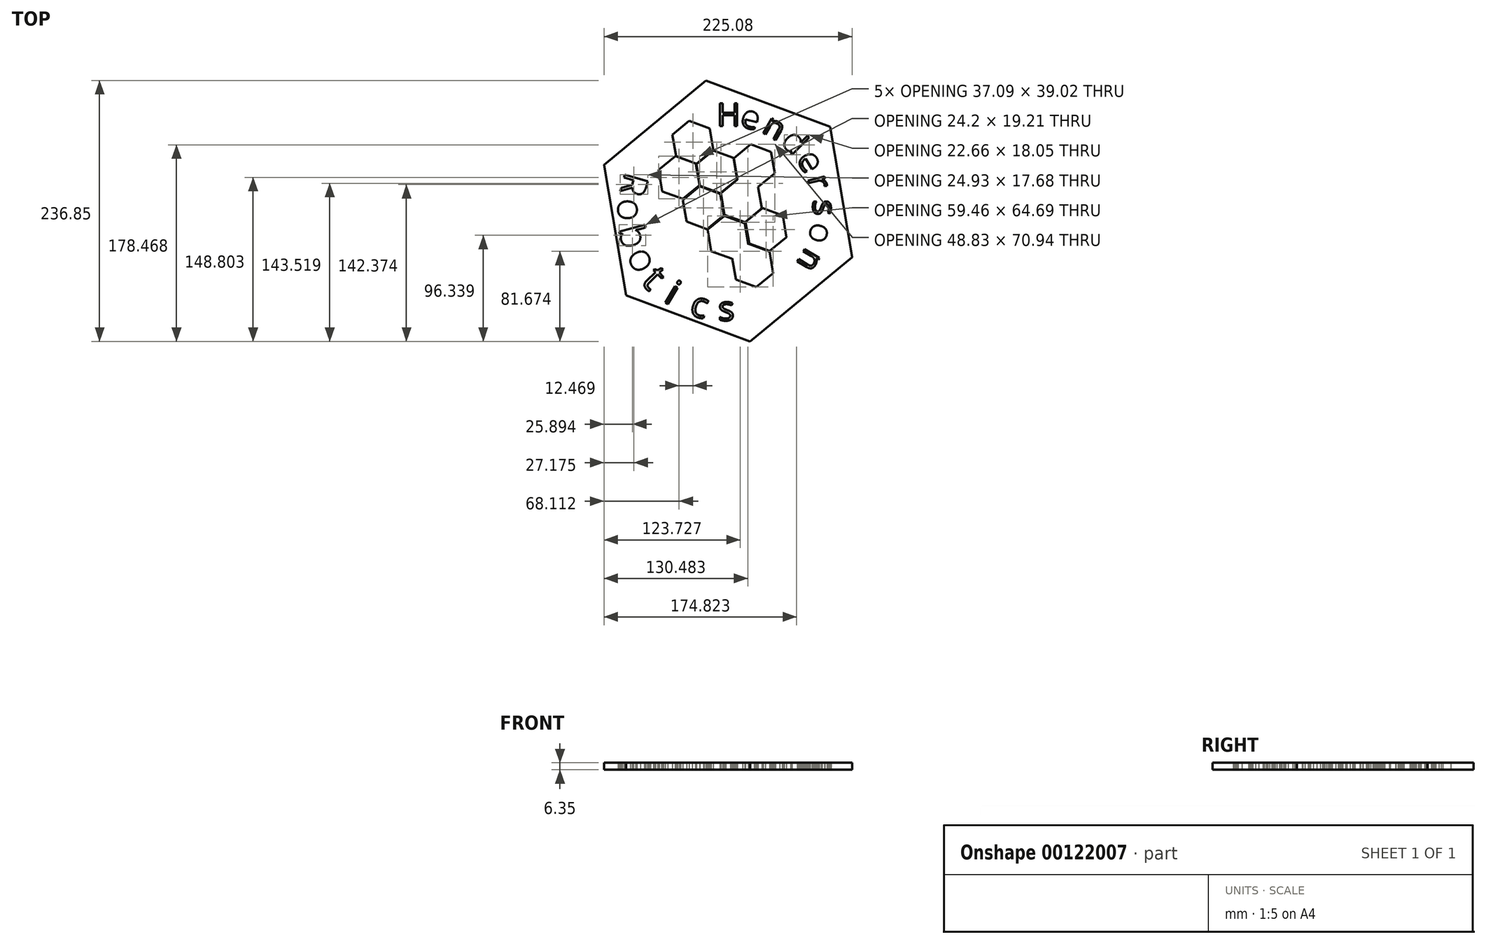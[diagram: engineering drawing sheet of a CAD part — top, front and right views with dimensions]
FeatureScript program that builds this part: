
annotation { "Feature Type Name" : "Feature", "Feature Type Description" : "" }
export const myFeature = defineFeature(function(context is Context, id is Id, definition is map)
    precondition{}
    {
        {
            var Q0;
            Q0=qCreatedBy(makeId("Top.planeOp"),FACE);
            var sketch = newSketch(context, id + "F0", { "sketchPlane" : qUnion([Q0])});
            skLineSegment(sketch, "E0.5.0", {"start": v(-77.17, 34.08) * mm, "end": v(-71.91, 53.7) * mm});
            skLineSegment(sketch, "E0.7.0", {"start": v(-71.91, -5.87) * mm, "end": v(-77.17, 13.76) * mm});
            skPoint(sketch, "E0.center", {"position": v(0, 23.92) * mm});
            skText(sketch, "E1", { "text": "H", "fontName": "OpenSans-Regular.ttf"});
            skText(sketch, "E2", { "text": "e", "fontName": "OpenSans-Regular.ttf"});
            skText(sketch, "E3", { "text": "n", "fontName": "OpenSans-Regular.ttf"});
            skText(sketch, "E4", { "text": "d", "fontName": "OpenSans-Regular.ttf"});
            skText(sketch, "E5", { "text": "e", "fontName": "OpenSans-Regular.ttf"});
            skText(sketch, "E6", { "text": "r", "fontName": "OpenSans-Regular.ttf"});
            skText(sketch, "E7", { "text": "s", "fontName": "OpenSans-Regular.ttf"});
            skText(sketch, "E8", { "text": "o", "fontName": "OpenSans-Regular.ttf"});
            skText(sketch, "E9", { "text": "s", "fontName": "OpenSans-Regular.ttf"});
            skText(sketch, "E10", { "text": "c", "fontName": "OpenSans-Regular.ttf"});
            skText(sketch, "E11", { "text": "i", "fontName": "OpenSans-Regular.ttf"});
            skText(sketch, "E12", { "text": "t", "fontName": "OpenSans-Regular.ttf"});
            skText(sketch, "E13", { "text": "o", "fontName": "OpenSans-Regular.ttf"});
            skText(sketch, "E14", { "text": "b", "fontName": "OpenSans-Regular.ttf"});
            skText(sketch, "E15", { "text": "o", "fontName": "OpenSans-Regular.ttf"});
            skText(sketch, "E16", { "text": "R", "fontName": "OpenSans-Regular.ttf"});
            skText(sketch, "E17", { "text": "n", "fontName": "OpenSans-Regular.ttf"});
            skCircle(sketch, "E18.cCircle", {"center": v(0, 23.92) * mm, "radius": 104 * mm, "construction": true});
            skLineSegment(sketch, "E18.0", {"start": v(92.58, 100.41) * mm, "end": v(112.54, -18.01) * mm});
            skLineSegment(sketch, "E18.1", {"start": v(112.54, -18.01) * mm, "end": v(19.96, -94.5) * mm});
            skLineSegment(sketch, "E18.2", {"start": v(19.96, -94.5) * mm, "end": v(-92.58, -52.58) * mm});
            skLineSegment(sketch, "E18.3", {"start": v(-92.58, -52.58) * mm, "end": v(-112.54, 65.85) * mm});
            skLineSegment(sketch, "E18.4", {"start": v(-112.54, 65.85) * mm, "end": v(-19.96, 142.34) * mm});
            skLineSegment(sketch, "E18.5", {"start": v(-19.96, 142.34) * mm, "end": v(92.58, 100.41) * mm});
            skPoint(sketch, "E18.0.midPoint", {"position": v(102.56, 41.2) * mm});
            skCircle(sketch, "E19.cCircle", {"center": v(-10.25, 59.37) * mm, "radius": 17.14 * mm, "construction": true});
            skLineSegment(sketch, "E19.0", {"start": v(8.29, 52.47) * mm, "end": v(-6.96, 39.86) * mm});
            skLineSegment(sketch, "E19.1", {"start": v(-6.96, 39.86) * mm, "end": v(-25.5, 46.77) * mm});
            skLineSegment(sketch, "E19.2", {"start": v(-25.5, 46.77) * mm, "end": v(-28.8, 66.28) * mm});
            skLineSegment(sketch, "E19.3", {"start": v(-28.8, 66.28) * mm, "end": v(-13.54, 78.89) * mm});
            skLineSegment(sketch, "E19.4", {"start": v(-13.54, 78.89) * mm, "end": v(5, 71.98) * mm});
            skLineSegment(sketch, "E19.5", {"start": v(5, 71.98) * mm, "end": v(8.29, 52.47) * mm});
            skCircle(sketch, "E20.cCircle", {"center": v(12.07, 33.05) * mm, "radius": 17.14 * mm, "construction": true});
            skLineSegment(sketch, "E20.0", {"start": v(30.61, 26.14) * mm, "end": v(15.36, 13.54) * mm});
            skLineSegment(sketch, "E20.1", {"start": v(15.36, 13.54) * mm, "end": v(-3.18, 20.44) * mm});
            skLineSegment(sketch, "E20.2", {"start": v(-3.18, 20.44) * mm, "end": v(-6.47, 39.96) * mm});
            skLineSegment(sketch, "E20.3", {"start": v(-6.47, 39.96) * mm, "end": v(8.78, 52.56) * mm});
            skLineSegment(sketch, "E20.4", {"start": v(8.78, 52.56) * mm, "end": v(27.32, 45.65) * mm});
            skLineSegment(sketch, "E20.5", {"start": v(27.32, 45.65) * mm, "end": v(30.61, 26.14) * mm});
            skCircle(sketch, "E21.cCircle", {"center": v(0, 0) * mm, "radius": 17.14 * mm, "construction": true});
            skLineSegment(sketch, "E21.0", {"start": v(15.25, 12.6) * mm, "end": v(18.54, -6.9) * mm});
            skLineSegment(sketch, "E21.1", {"start": v(18.54, -6.9) * mm, "end": v(3.3, -19.51) * mm});
            skLineSegment(sketch, "E21.2", {"start": v(3.3, -19.51) * mm, "end": v(-15.25, -12.6) * mm});
            skLineSegment(sketch, "E21.3", {"start": v(-15.25, -12.6) * mm, "end": v(-18.54, 6.9) * mm});
            skLineSegment(sketch, "E21.4", {"start": v(-18.54, 6.9) * mm, "end": v(-3.3, 19.51) * mm});
            skLineSegment(sketch, "E21.5", {"start": v(-3.3, 19.51) * mm, "end": v(15.25, 12.6) * mm});
            skCircle(sketch, "E22.cCircle", {"center": v(-22.42, 26.8) * mm, "radius": 17.14 * mm, "construction": true});
            skLineSegment(sketch, "E22.0", {"start": v(-19.13, 7.3) * mm, "end": v(-37.67, 14.2) * mm});
            skLineSegment(sketch, "E22.1", {"start": v(-37.67, 14.2) * mm, "end": v(-40.96, 33.72) * mm});
            skLineSegment(sketch, "E22.2", {"start": v(-40.96, 33.72) * mm, "end": v(-25.7, 46.32) * mm});
            skLineSegment(sketch, "E22.3", {"start": v(-25.7, 46.32) * mm, "end": v(-7.17, 39.42) * mm});
            skLineSegment(sketch, "E22.4", {"start": v(-7.17, 39.42) * mm, "end": v(-3.88, 19.9) * mm});
            skLineSegment(sketch, "E22.5", {"start": v(-3.88, 19.9) * mm, "end": v(-19.13, 7.3) * mm});
            skCircle(sketch, "E23.cCircle", {"center": v(34.45, 7) * mm, "radius": 17.14 * mm, "construction": true});
            skLineSegment(sketch, "E23.0", {"start": v(53, 0.1) * mm, "end": v(37.74, -12.52) * mm});
            skLineSegment(sketch, "E23.1", {"start": v(37.74, -12.52) * mm, "end": v(19.2, -5.6) * mm});
            skLineSegment(sketch, "E23.2", {"start": v(19.2, -5.6) * mm, "end": v(15.91, 13.9) * mm});
            skLineSegment(sketch, "E23.3", {"start": v(15.91, 13.9) * mm, "end": v(31.16, 26.5) * mm});
            skLineSegment(sketch, "E23.4", {"start": v(31.16, 26.5) * mm, "end": v(49.7, 19.6) * mm});
            skLineSegment(sketch, "E23.5", {"start": v(49.7, 19.6) * mm, "end": v(53, 0.1) * mm});
            skPoint(sketch, "E23.0.midPoint", {"position": v(45.37, -6.21) * mm});
            skPoint(sketch, "E24", {"position": v(-4.95, 101.1) * mm});
            skPoint(sketch, "E25", {"position": v(5.85, 101.1) * mm});
            skPoint(sketch, "E26", {"position": v(8.32, 101.1) * mm});
            skPoint(sketch, "E27", {"position": v(-7.37, 101.1) * mm});
            skLineSegment(sketch, "E28", {"start": v(8.32, 101.1) * mm, "end": v(10.16, 101.1) * mm});
            skLineSegment(sketch, "E29", {"start": v(-7.37, 101.1) * mm, "end": v(-10.16, 101.1) * mm});
            skCircle(sketch, "E30.cCircle", {"center": v(-33.8, -5.48) * mm, "radius": 17.14 * mm, "construction": true});
            skLineSegment(sketch, "E30.0", {"start": v(-15.25, -12.39) * mm, "end": v(-30.5, -25) * mm, "construction": true});
            skLineSegment(sketch, "E30.1", {"start": v(-30.5, -25) * mm, "end": v(-49.05, -18.09) * mm, "construction": true});
            skLineSegment(sketch, "E30.2", {"start": v(-49.05, -18.09) * mm, "end": v(-52.34, 1.43) * mm, "construction": true});
            skLineSegment(sketch, "E30.3", {"start": v(-52.34, 1.43) * mm, "end": v(-37.08, 14.03) * mm, "construction": true});
            skLineSegment(sketch, "E30.4", {"start": v(-37.08, 14.03) * mm, "end": v(-18.54, 7.12) * mm, "construction": true});
            skLineSegment(sketch, "E30.5", {"start": v(-18.54, 7.12) * mm, "end": v(-15.25, -12.39) * mm, "construction": true});
            skPoint(sketch, "E30.0.midPoint", {"position": v(-22.88, -18.69) * mm});
            skCircle(sketch, "E31.cCircle", {"center": v(-44.43, 54.3) * mm, "radius": 17.14 * mm, "construction": true});
            skLineSegment(sketch, "E31.0", {"start": v(-25.89, 47.39) * mm, "end": v(-41.14, 34.78) * mm});
            skLineSegment(sketch, "E31.1", {"start": v(-41.14, 34.78) * mm, "end": v(-59.68, 41.69) * mm});
            skLineSegment(sketch, "E31.2", {"start": v(-59.68, 41.69) * mm, "end": v(-62.97, 61.2) * mm});
            skLineSegment(sketch, "E31.3", {"start": v(-62.97, 61.2) * mm, "end": v(-47.72, 73.8) * mm});
            skLineSegment(sketch, "E31.4", {"start": v(-47.72, 73.8) * mm, "end": v(-29.18, 66.9) * mm});
            skLineSegment(sketch, "E31.5", {"start": v(-29.18, 66.9) * mm, "end": v(-25.89, 47.39) * mm});
            skPoint(sketch, "E31.0.midPoint", {"position": v(-33.51, 41.08) * mm});
            skCircle(sketch, "E32.cCircle", {"center": v(23.81, 64.97) * mm, "radius": 17.14 * mm, "construction": true});
            skLineSegment(sketch, "E32.0", {"start": v(42.36, 58.06) * mm, "end": v(27.1, 45.46) * mm});
            skLineSegment(sketch, "E32.1", {"start": v(27.1, 45.46) * mm, "end": v(8.56, 52.36) * mm});
            skLineSegment(sketch, "E32.2", {"start": v(8.56, 52.36) * mm, "end": v(5.27, 71.87) * mm});
            skLineSegment(sketch, "E32.3", {"start": v(5.27, 71.87) * mm, "end": v(20.52, 84.48) * mm});
            skLineSegment(sketch, "E32.4", {"start": v(20.52, 84.48) * mm, "end": v(39.07, 77.57) * mm});
            skLineSegment(sketch, "E32.5", {"start": v(39.07, 77.57) * mm, "end": v(42.36, 58.06) * mm});
            skPoint(sketch, "E32.0.midPoint", {"position": v(34.73, 51.76) * mm});
            skCircle(sketch, "E33.cCircle", {"center": v(22.37, -25.67) * mm, "radius": 17.14 * mm, "construction": true});
            skLineSegment(sketch, "E33.0", {"start": v(40.92, -32.58) * mm, "end": v(25.66, -45.18) * mm});
            skLineSegment(sketch, "E33.1", {"start": v(25.66, -45.18) * mm, "end": v(7.12, -38.28) * mm});
            skLineSegment(sketch, "E33.2", {"start": v(7.12, -38.28) * mm, "end": v(3.83, -18.77) * mm});
            skLineSegment(sketch, "E33.3", {"start": v(3.83, -18.77) * mm, "end": v(19.08, -6.16) * mm});
            skLineSegment(sketch, "E33.4", {"start": v(19.08, -6.16) * mm, "end": v(37.63, -13.07) * mm});
            skLineSegment(sketch, "E33.5", {"start": v(37.63, -13.07) * mm, "end": v(40.92, -32.58) * mm});
            skPoint(sketch, "E33.0.midPoint", {"position": v(33.3, -38.88) * mm});
            skCircle(sketch, "E34.cCircle", {"center": v(-31.96, 86.25) * mm, "radius": 17.14 * mm, "construction": true});
            skLineSegment(sketch, "E34.0", {"start": v(-13.42, 79.34) * mm, "end": v(-28.67, 66.74) * mm});
            skLineSegment(sketch, "E34.1", {"start": v(-28.67, 66.74) * mm, "end": v(-47.21, 73.64) * mm});
            skLineSegment(sketch, "E34.2", {"start": v(-47.21, 73.64) * mm, "end": v(-50.5, 93.16) * mm});
            skLineSegment(sketch, "E34.3", {"start": v(-50.5, 93.16) * mm, "end": v(-35.25, 105.76) * mm});
            skLineSegment(sketch, "E34.4", {"start": v(-35.25, 105.76) * mm, "end": v(-16.7, 98.86) * mm});
            skLineSegment(sketch, "E34.5", {"start": v(-16.7, 98.86) * mm, "end": v(-13.42, 79.34) * mm});
            skPoint(sketch, "E34.0.midPoint", {"position": v(-21.04, 73.04) * mm});
            const initialGuessF0  = {"E1": [-0.01016, 0.1011, 1, 0, 0.02075], "E2": [0.01016, 0.1011, 0.96593, -0.25882, 0.02075], "E3": [0.02979, 0.09583, 0.86603, -0.5, 0.02075], "E4": [0.04739, 0.08567, 0.7071, -0.7071, 0.02075], "E5": [0.06175, 0.0713, 0.5, -0.86603, 0.0218], "E6": [0.07191, 0.0537, 0.25882, -0.96593, 0.02075], "E7": [0.07717, 0.03408, 0, -1, 0.02152], "E8": [0.07717, 0.01376, -0.25882, -0.96593, 0.01967], "E9": [-0.00894, -0.07554, 1, -0.00234, 0.02232], "E10": [-0.03578, -0.0703, 0.96573, -0.25954, 0.0231], "E11": [-0.0593, -0.0579, 0.85963, -0.51091, 0.02334], "E12": [-0.07973, -0.04072, 0.69232, -0.72159, 0.02491], "E13": [-0.09193, -0.01688, 0.48182, -0.87627, 0.02284], "E14": [-0.09946, 0.00776, 0.25997, -0.96562, 0.02308], "E15": [-0.0994, 0.03443, -0.01576, -0.99988, 0.02223], "E16": [-0.09294, 0.05957, -0.26856, -0.96326, 0.02182], "E17": [0.07069, -0.00851, -0.5129, -0.85845, 0.02097]};
            skSetInitialGuess(sketch, initialGuessF0);
            skSolve(sketch);
        }
        {
            var Q0;
            Q0=makeQuery(id+"F0.imprint","IMPRINT",FACE,{"disambiguationData":[TD([[makeQuery(id+"F0.imprint","IMPRINT",EDGE,{"derivedFrom":sQuery(id+"F0.wireOp",EDGE,"E1.sketch_text.stroke-0")}),1.0]])]});
            extrude(context, id + "F1", {"entities" : qUnion([Q0]), "depth" : 6.35 * mm});
        }
    });
